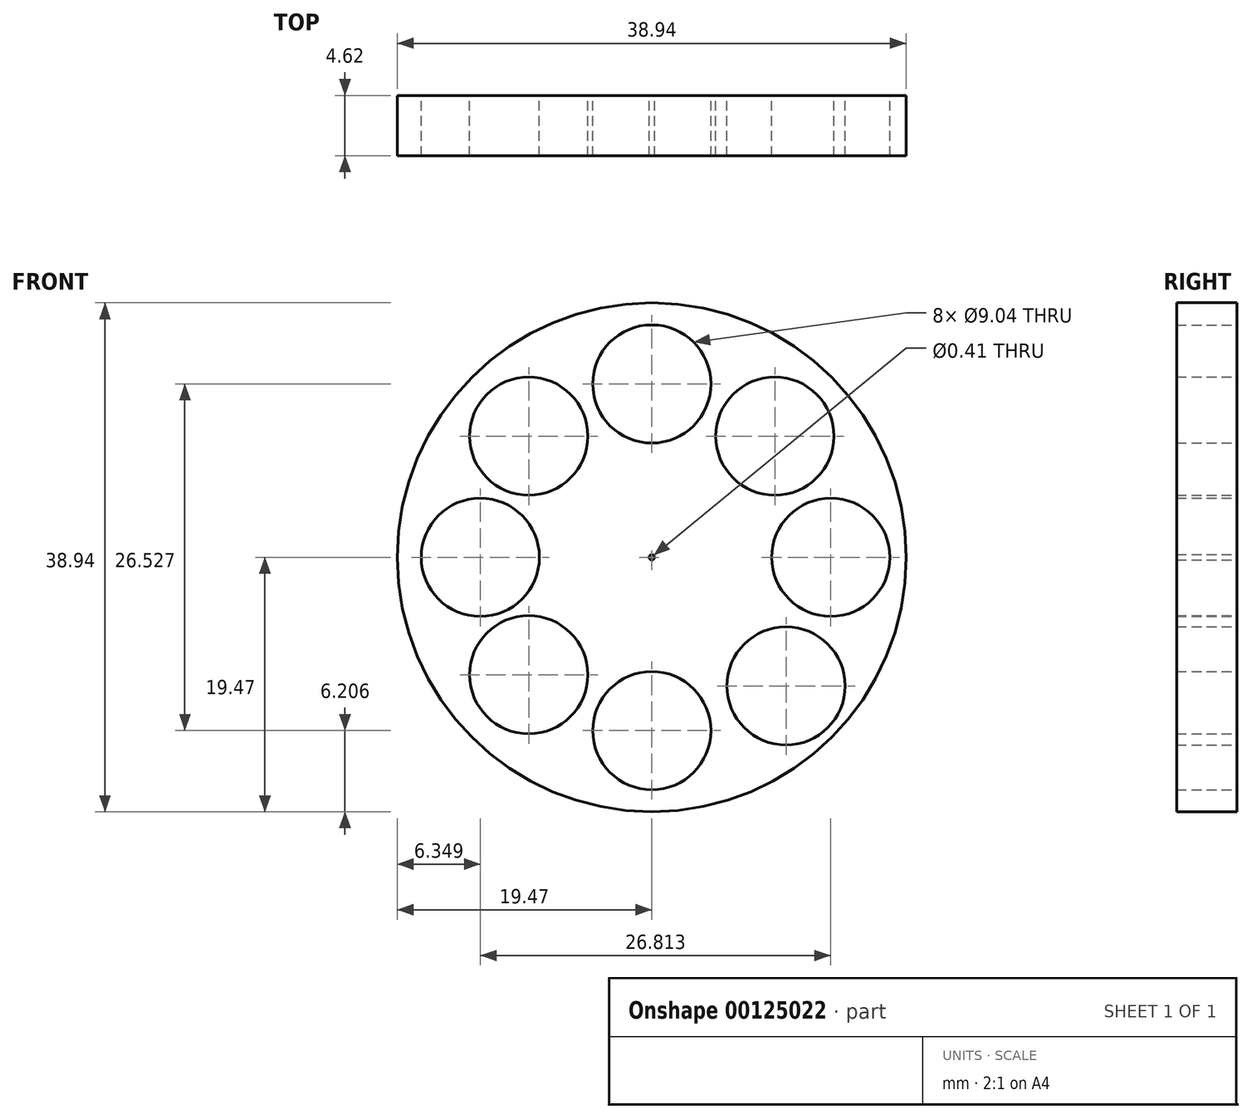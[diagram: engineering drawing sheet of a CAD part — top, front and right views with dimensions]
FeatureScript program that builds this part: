
annotation { "Feature Type Name" : "Feature", "Feature Type Description" : "" }
export const myFeature = defineFeature(function(context is Context, id is Id, definition is map)
    precondition{}
    {
        {
            var Q0;
            Q0=qCreatedBy(makeId("Front.planeOp"),FACE);
            var sketch = newSketch(context, id + "F0", { "sketchPlane" : qUnion([Q0])});
            skCircle(sketch, "E0", {"center": v(0, 0) * mm, "radius": 19.47 * mm});
            skCircle(sketch, "E1", {"center": v(0, 13.26) * mm, "radius": 4.52 * mm});
            skCircle(sketch, "E2", {"center": v(13.7, 0) * mm, "radius": 4.52 * mm});
            skCircle(sketch, "E3", {"center": v(9.41, 9.27) * mm, "radius": 4.52 * mm});
            skCircle(sketch, "E4", {"center": v(0, -13.26) * mm, "radius": 4.52 * mm});
            skCircle(sketch, "E5", {"center": v(-9.41, -8.99) * mm, "radius": 4.52 * mm});
            skCircle(sketch, "E6", {"center": v(-13.12, 0) * mm, "radius": 4.52 * mm});
            skCircle(sketch, "E7", {"center": v(-9.41, 9.27) * mm, "radius": 4.52 * mm});
            skCircle(sketch, "E8", {"center": v(10.27, -9.84) * mm, "radius": 4.52 * mm});
            skCircle(sketch, "E9", {"center": v(0, 0) * mm, "radius": 0.2 * mm});
            skSolve(sketch);
        }
        {
            var Q0;
            Q0=qCreatedBy(makeId("Right.planeOp"),FACE);
            var sketch = newSketch(context, id + "F1", { "sketchPlane" : qUnion([Q0])});
            skLineSegment(sketch, "E10", {"start": v(0, 0) * mm, "end": v(4.62, 0) * mm});
            skSolve(sketch);
        }
        {
            var Q0;
            Q0=makeQuery(id+"F0.imprint","IMPRINT",FACE,{"disambiguationData":[TD([[makeQuery(id+"F0.imprint","IMPRINT",EDGE,{"derivedFrom":sQuery(id+"F0.wireOp",EDGE,"E0")}),1.0]])]});
            var Q1;
            Q1=sQuery(id+"F1.wireOp",EDGE,"E10");
            sweep(context, id + "F2", {"profiles" : qUnion([Q0]), "path" : qUnion([Q1])});
        }
    });
